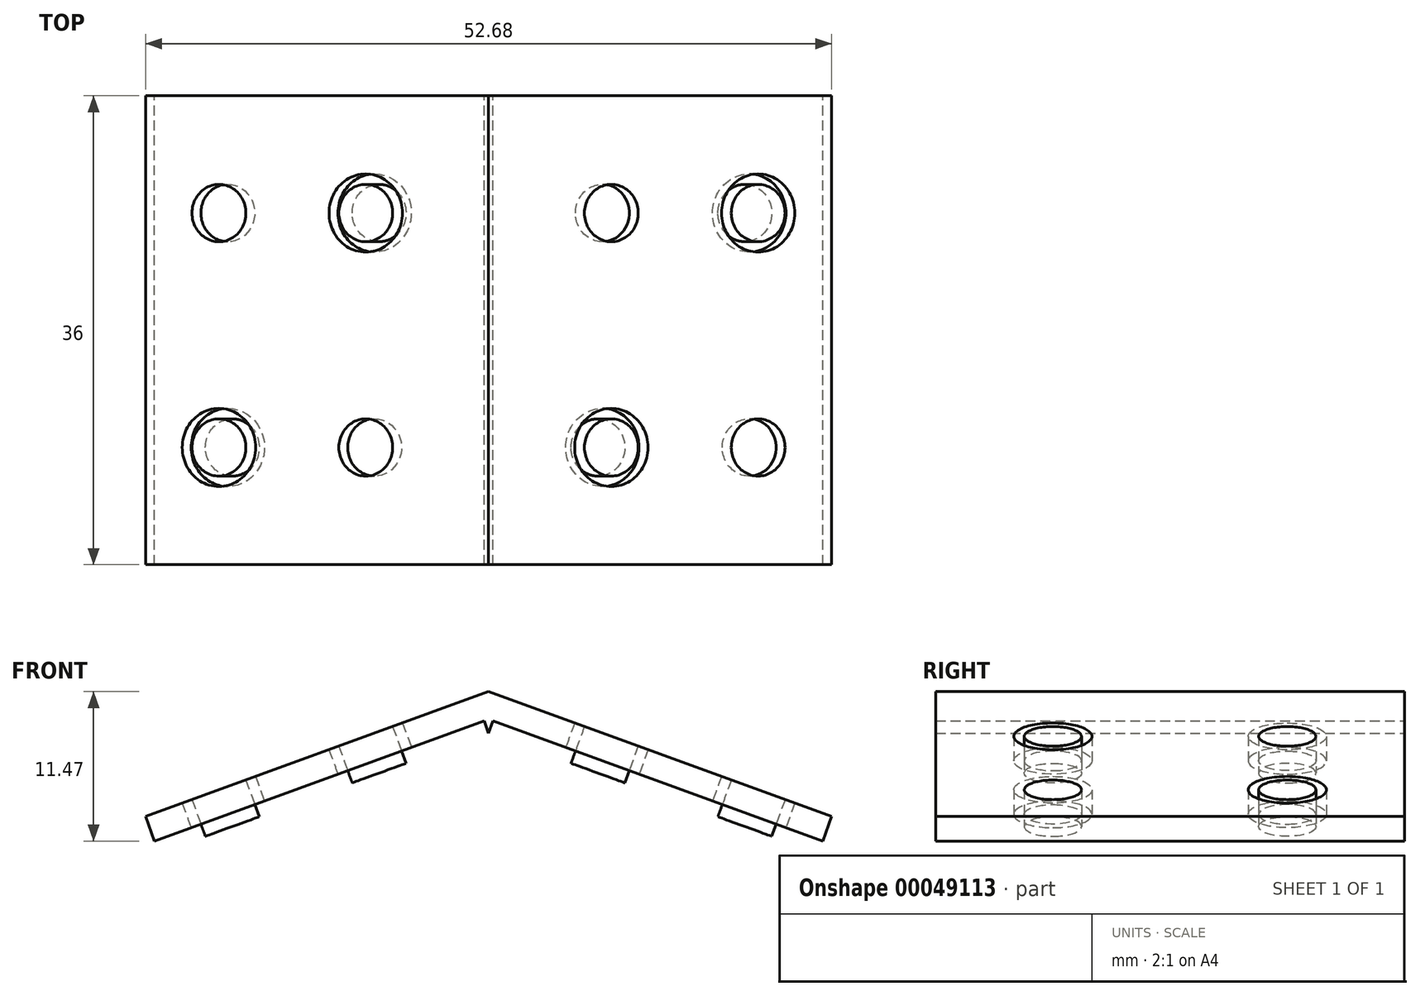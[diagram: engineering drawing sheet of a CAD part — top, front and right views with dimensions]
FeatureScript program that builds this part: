
annotation { "Feature Type Name" : "Feature", "Feature Type Description" : "" }
export const myFeature = defineFeature(function(context is Context, id is Id, definition is map)
    precondition{}
    {
        {
            var Q0;
            Q0=qCreatedBy(makeId("Front.planeOp"),FACE);
            var sketch = newSketch(context, id + "F0", { "sketchPlane" : qUnion([Q0])});
            skLineSegment(sketch, "E0", {"start": v(-38.34, -30.76) * mm, "end": v(-12, -21.17) * mm, "construction": true});
            skLineSegment(sketch, "E1", {"start": v(14.34, -30.76) * mm, "end": v(-12, -21.17) * mm, "construction": true});
            skPoint(sketch, "E2", {"position": v(-12, -21.17) * mm});
            skLineSegment(sketch, "E3", {"start": v(-38.34, -30.76) * mm, "end": v(-12, -21.17) * mm});
            skLineSegment(sketch, "E4", {"start": v(-12, -21.17) * mm, "end": v(14.34, -30.76) * mm});
            skLineSegment(sketch, "E5.0", {"start": v(13.32, -33.58) * mm, "end": v(-12, -24.37) * mm});
            skLineSegment(sketch, "E5.1", {"start": v(-37.32, -33.58) * mm, "end": v(-12, -24.37) * mm});
            skLineSegment(sketch, "E6", {"start": v(-38.34, -30.76) * mm, "end": v(-37.32, -33.58) * mm});
            skLineSegment(sketch, "E7", {"start": v(14.34, -30.76) * mm, "end": v(13.32, -33.58) * mm});
            skSolve(sketch);
        }
        {
            var Q0;
            Q0=makeQuery(id+"F0.imprint","IMPRINT",FACE,{"disambiguationData":[TD([[makeQuery(id+"F0.imprint","IMPRINT",EDGE,{"derivedFrom":sQuery(id+"F0.wireOp",EDGE,"E3")}),-1.0]])]});
            extrude(context, id + "F1", {"entities" : qUnion([Q0]), "depth" : 36 * mm});
        }
        {
            var Q0;
            Q0=makeQuery(id+"F1.opExtrude","SWEPT_FACE",FACE,{"disambiguationData":[OSD([sQuery(id+"F0.wireOp",EDGE,"E5.1")])]});
            var sketch = newSketch(context, id + "F2", { "sketchPlane" : qUnion([Q0])});
            skPoint(sketch, "E8", {"position": v(-22.55, 36) * mm});
            skPoint(sketch, "E9", {"position": v(-46.55, 36) * mm});
            skPoint(sketch, "E10", {"position": v(-34.55, 36) * mm});
            skLineSegment(sketch, "E11", {"start": v(-22.55, 36) * mm, "end": v(-22.55, 0) * mm, "construction": true});
            skLineSegment(sketch, "E12", {"start": v(-34.55, 36) * mm, "end": v(-34.55, 0) * mm, "construction": true});
            skLineSegment(sketch, "E13", {"start": v(-46.55, 18) * mm, "end": v(-22.55, 18) * mm, "construction": true});
            skPoint(sketch, "E14", {"position": v(-34.55, 27) * mm});
            skLineSegment(sketch, "E15", {"start": v(-34.55, 27) * mm, "end": v(-22.55, 27) * mm, "construction": true});
            skPoint(sketch, "E16", {"position": v(-28.55, 27) * mm});
            skCircle(sketch, "E17", {"center": v(-28.55, 27) * mm, "radius": 3 * mm});
            skCircle(sketch, "E18", {"center": v(-28.55, 27) * mm, "radius": 2.2 * mm});
            skCircle(sketch, "E19.MirrorC", {"center": v(-40.55, 27) * mm, "radius": 3 * mm});
            skCircle(sketch, "E20.MirrorC", {"center": v(-40.55, 27) * mm, "radius": 2.2 * mm});
            skCircle(sketch, "E21.MirrorC", {"center": v(-40.55, 9) * mm, "radius": 3 * mm});
            skCircle(sketch, "E22.MirrorC", {"center": v(-40.55, 9) * mm, "radius": 2.2 * mm});
            skCircle(sketch, "E23.MirrorC", {"center": v(-28.55, 9) * mm, "radius": 3 * mm});
            skCircle(sketch, "E24.MirrorC", {"center": v(-28.55, 9) * mm, "radius": 2.2 * mm});
            skSolve(sketch);
        }
        {
            var Q0;
            Q0=makeQuery(id+"F2.imprint","IMPRINT",FACE,{"disambiguationData":[TD([[makeQuery(id+"F2.imprint","IMPRINT",EDGE,{"derivedFrom":sQuery(id+"F2.wireOp",EDGE,"E20.MirrorC")}),-1.0]])]});
            var Q1;
            Q1=makeQuery(id+"F2.imprint","IMPRINT",FACE,{"disambiguationData":[TD([[makeQuery(id+"F2.imprint","IMPRINT",EDGE,{"derivedFrom":sQuery(id+"F2.wireOp",EDGE,"E18")}),1.0]])]});
            var Q2;
            Q2=makeQuery(id+"F2.imprint","IMPRINT",FACE,{"disambiguationData":[TD([[makeQuery(id+"F2.imprint","IMPRINT",EDGE,{"derivedFrom":sQuery(id+"F2.wireOp",EDGE,"E24.MirrorC")}),-1.0]])]});
            var Q3;
            Q3=makeQuery(id+"F2.imprint","IMPRINT",FACE,{"disambiguationData":[TD([[makeQuery(id+"F2.imprint","IMPRINT",EDGE,{"derivedFrom":sQuery(id+"F2.wireOp",EDGE,"E22.MirrorC")}),1.0]])]});
            extrude(context, id + "F3", {"entities" : qUnion([Q0, Q1, Q2, Q3]), "operationType" : NewBodyOperationType.REMOVE, "endBound" : BoundingType.THROUGH_ALL, "oppositeDirection" : true, "depth" : 25 * mm});
        }
        {
            var Q0;
            Q0=makeQuery(id+"F2.imprint","IMPRINT",FACE,{"disambiguationData":[TD([[makeQuery(id+"F2.imprint","IMPRINT",EDGE,{"derivedFrom":sQuery(id+"F2.wireOp",EDGE,"E19.MirrorC")}),-1.0]])]});
            var Q1;
            Q1=makeQuery(id+"F2.imprint","IMPRINT",FACE,{"disambiguationData":[TD([[makeQuery(id+"F2.imprint","IMPRINT",EDGE,{"derivedFrom":sQuery(id+"F2.wireOp",EDGE,"E21.MirrorC")}),1.0]])]});
            var Q2;
            Q2=makeQuery(id+"F2.imprint","IMPRINT",FACE,{"disambiguationData":[TD([[makeQuery(id+"F2.imprint","IMPRINT",EDGE,{"derivedFrom":sQuery(id+"F2.wireOp",EDGE,"E23.MirrorC")}),-1.0]])]});
            var Q3;
            Q3=makeQuery(id+"F2.imprint","IMPRINT",FACE,{"disambiguationData":[TD([[makeQuery(id+"F2.imprint","IMPRINT",EDGE,{"derivedFrom":sQuery(id+"F2.wireOp",EDGE,"E17")}),1.0]])]});
            extrude(context, id + "F4", {"entities" : qUnion([Q0, Q1, Q2, Q3]), "operationType" : NewBodyOperationType.REMOVE, "oppositeDirection" : true, "depth" : 1 * mm});
        }
        {
            var Q0;
            Q0=makeQuery(id+"F1.opExtrude","SWEPT_FACE",FACE,{"disambiguationData":[OSD([sQuery(id+"F0.wireOp",EDGE,"E5.0")])]});
            var sketch = newSketch(context, id + "F5", { "sketchPlane" : qUnion([Q0])});
            skPoint(sketch, "E25", {"position": v(0, 36) * mm});
            skPoint(sketch, "E26", {"position": v(24, 36) * mm});
            skLineSegment(sketch, "E27", {"start": v(0, 36) * mm, "end": v(0, 0) * mm, "construction": true});
            skLineSegment(sketch, "E28", {"start": v(24, 18) * mm, "end": v(0, 18) * mm, "construction": true});
            skPoint(sketch, "E29", {"position": v(12, 18) * mm});
            skLineSegment(sketch, "E30", {"start": v(12, 36) * mm, "end": v(12, 0) * mm, "construction": true});
            skPoint(sketch, "E31", {"position": v(12, 27) * mm});
            skLineSegment(sketch, "E32", {"start": v(12, 27) * mm, "end": v(24, 27) * mm, "construction": true});
            skPoint(sketch, "E33", {"position": v(18, 27) * mm});
            skCircle(sketch, "E34", {"center": v(18, 27) * mm, "radius": 3 * mm});
            skCircle(sketch, "E35", {"center": v(18, 27) * mm, "radius": 2.2 * mm});
            skCircle(sketch, "E36.MirrorC", {"center": v(6, 27) * mm, "radius": 3 * mm});
            skCircle(sketch, "E37.MirrorC", {"center": v(6, 27) * mm, "radius": 2.2 * mm});
            skCircle(sketch, "E38.MirrorC", {"center": v(6, 9) * mm, "radius": 3 * mm});
            skCircle(sketch, "E39.MirrorC", {"center": v(6, 9) * mm, "radius": 2.2 * mm});
            skCircle(sketch, "E40.MirrorC", {"center": v(18, 9) * mm, "radius": 3 * mm});
            skCircle(sketch, "E41.MirrorC", {"center": v(18, 9) * mm, "radius": 2.2 * mm});
            skSolve(sketch);
        }
        {
            var Q0;
            Q0=makeQuery(id+"F5.imprint","IMPRINT",FACE,{"disambiguationData":[TD([[makeQuery(id+"F5.imprint","IMPRINT",EDGE,{"derivedFrom":sQuery(id+"F5.wireOp",EDGE,"E37.MirrorC")}),-1.0]])]});
            var Q1;
            Q1=makeQuery(id+"F5.imprint","IMPRINT",FACE,{"disambiguationData":[TD([[makeQuery(id+"F5.imprint","IMPRINT",EDGE,{"derivedFrom":sQuery(id+"F5.wireOp",EDGE,"E35")}),1.0]])]});
            var Q2;
            Q2=makeQuery(id+"F5.imprint","IMPRINT",FACE,{"disambiguationData":[TD([[makeQuery(id+"F5.imprint","IMPRINT",EDGE,{"derivedFrom":sQuery(id+"F5.wireOp",EDGE,"E39.MirrorC")}),1.0]])]});
            var Q3;
            Q3=makeQuery(id+"F5.imprint","IMPRINT",FACE,{"disambiguationData":[TD([[makeQuery(id+"F5.imprint","IMPRINT",EDGE,{"derivedFrom":sQuery(id+"F5.wireOp",EDGE,"E41.MirrorC")}),-1.0]])]});
            extrude(context, id + "F6", {"entities" : qUnion([Q0, Q1, Q2, Q3]), "operationType" : NewBodyOperationType.REMOVE, "endBound" : BoundingType.THROUGH_ALL, "oppositeDirection" : true, "depth" : 25 * mm});
        }
        {
            var Q0;
            Q0=makeQuery(id+"F5.imprint","IMPRINT",FACE,{"disambiguationData":[TD([[makeQuery(id+"F5.imprint","IMPRINT",EDGE,{"derivedFrom":sQuery(id+"F5.wireOp",EDGE,"E36.MirrorC")}),-1.0]])]});
            var Q1;
            Q1=makeQuery(id+"F5.imprint","IMPRINT",FACE,{"disambiguationData":[TD([[makeQuery(id+"F5.imprint","IMPRINT",EDGE,{"derivedFrom":sQuery(id+"F5.wireOp",EDGE,"E34")}),1.0]])]});
            var Q2;
            Q2=makeQuery(id+"F5.imprint","IMPRINT",FACE,{"disambiguationData":[TD([[makeQuery(id+"F5.imprint","IMPRINT",EDGE,{"derivedFrom":sQuery(id+"F5.wireOp",EDGE,"E40.MirrorC")}),-1.0]])]});
            var Q3;
            Q3=makeQuery(id+"F5.imprint","IMPRINT",FACE,{"disambiguationData":[TD([[makeQuery(id+"F5.imprint","IMPRINT",EDGE,{"derivedFrom":sQuery(id+"F5.wireOp",EDGE,"E38.MirrorC")}),1.0]])]});
            extrude(context, id + "F7", {"entities" : qUnion([Q0, Q1, Q2, Q3]), "operationType" : NewBodyOperationType.REMOVE, "oppositeDirection" : true, "depth" : 1 * mm});
        }
    });
